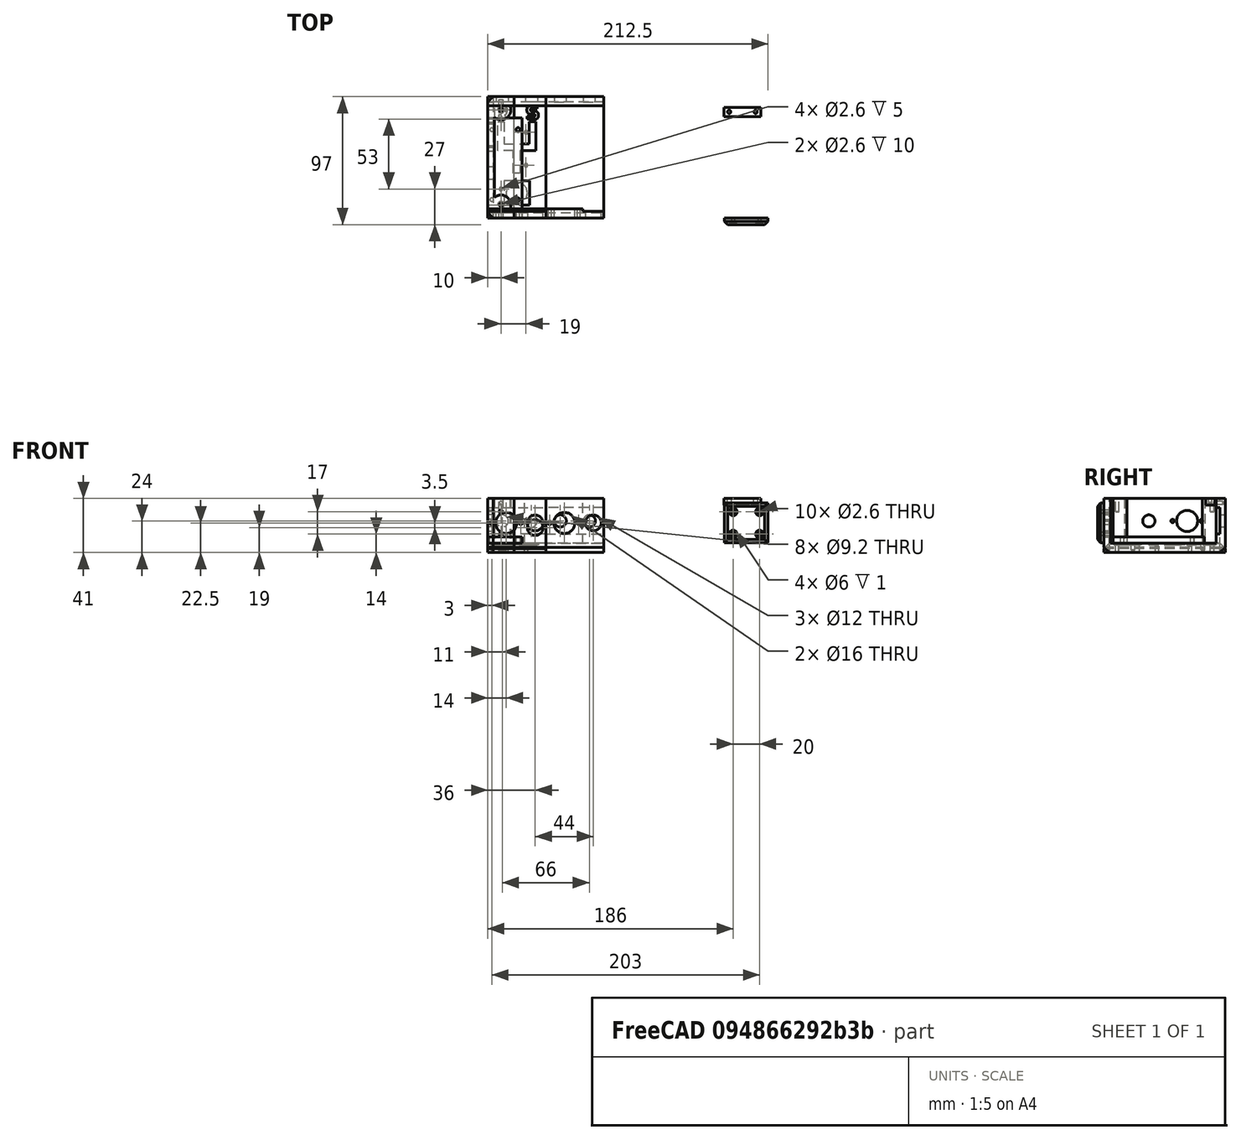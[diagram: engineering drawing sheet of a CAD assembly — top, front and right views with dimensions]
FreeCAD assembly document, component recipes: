
FREECAD ASSEMBLY — COMPONENT RECIPES ("loop-switcher")

This assembly document has 20 components, labeled P0..P19 below (a component is one placed body or linked part). 19 of them carry a construction recipe — the FreeCAD feature program that regenerates the part from scratch, quoted from this document or its linked companion documents; the rest are supplied as boundary geometry only. No exploded tour is included for this assembly.
COMPONENT P0 — recipe-attached ("base-module001", modeled in this document).
Construction recipe (the document's own serialized feature program — sketch geometry with constraints, then the solid features built on it; lengths are millimeters unless a unit is written):

FEATURE [Sketcher::SketchObject] Sketch
  ArcFitTolerance = 1e-06
  AttachmentSupport = -> [XY_Plane]
  FullyConstrained = true
  MakeInternals = false
  MapMode = 5
  sketch-geometry (4):
    g0: LineSegment StartX=0 StartY=0 StartZ=0 EndX=44 EndY=0 EndZ=0
    g1: LineSegment StartX=44 StartY=0 StartZ=0 EndX=44 EndY=92 EndZ=0
    g2: LineSegment StartX=44 StartY=92 StartZ=0 EndX=0 EndY=92 EndZ=0
    g3: LineSegment StartX=0 StartY=92 StartZ=0 EndX=0 EndY=0 EndZ=0
  constraints (11):
    c: Coincident(g0,g1)
    c: Coincident(g1,g2)
    c: Coincident(g2,g3)
    c: Coincident(g3,g0)
    c: Horizontal(g0)
    c: Horizontal(g2)
    c: Vertical(g1)
    c: Vertical(g3)
    c: Distance(g1,g3) = 44
    c: Distance(g0,g2) = 92
    c: Coincident(g0,g-1)
FEATURE [PartDesign::Pad] Pad
  Direction = (0,0,1)
  Length = 7
  Length2 = 10
  Profile = -> Sketch
  ReferenceAxis = -> Sketch [N_Axis]
  Refine = true
  Suppressed = false
  Type = 0
FEATURE [Sketcher::SketchObject] Sketch001
  ArcFitTolerance = 1e-06
  AttachmentSupport = -> [Pad]
  ExternalGeometry = -> [Pad]
  FullyConstrained = true
  MakeInternals = false
  MapMode = 5
  Placement = pos=(0,0,7) rot=(0,0,1;0rad)
  sketch-geometry (8):
    g0: LineSegment StartX=0 StartY=92 StartZ=0 EndX=0 EndY=85 EndZ=0
    g1: LineSegment StartX=0 StartY=85 StartZ=0 EndX=44 EndY=85 EndZ=0
    g2: LineSegment StartX=44 StartY=85 StartZ=0 EndX=44 EndY=92 EndZ=0
    g3: LineSegment StartX=44 StartY=92 StartZ=0 EndX=0 EndY=92 EndZ=0
    g4: LineSegment StartX=0 StartY=0 StartZ=0 EndX=44 EndY=0 EndZ=0
    g5: LineSegment StartX=44 StartY=0 StartZ=0 EndX=44 EndY=7 EndZ=0
    g6: LineSegment StartX=44 StartY=7 StartZ=0 EndX=0 EndY=7 EndZ=0
    g7: LineSegment StartX=0 StartY=7 StartZ=0 EndX=0 EndY=0 EndZ=0
  constraints (22):
    c: Coincident(g0,g1)
    c: Coincident(g1,g2)
    c: Coincident(g2,g3)
    c: Coincident(g3,g0)
    c: Vertical(g0)
    c: Vertical(g2)
    c: Horizontal(g1)
    c: Horizontal(g3)
    c: Distance(g0,g2) = 44
    c: Distance(g1,g3) = 7
    c: Coincident(g0,g-3)
    c: Coincident(g4,g5)
    c: Coincident(g5,g6)
    c: Coincident(g6,g7)
    c: Coincident(g7,g4)
    c: Horizontal(g4)
    c: Horizontal(g6)
    c: Vertical(g5)
    c: Vertical(g7)
    c: Distance(g5,g7) = 44
    c: Distance(g4,g6) = 7
    c: Coincident(g4,g-1)
FEATURE [PartDesign::Pad] Pad001
  BaseFeature = -> Pad
  Direction = (0,0,1)
  Length = 34
  Length2 = 10
  Profile = -> Sketch001
  ReferenceAxis = -> Sketch001 [N_Axis]
  Refine = true
  Suppressed = false
  Type = 0
FEATURE [Sketcher::SketchObject] Sketch002
  ArcFitTolerance = 1e-06
  AttachmentSupport = -> [Pad001]
  ExternalGeometry = -> [Pad001]
  FullyConstrained = true
  MakeInternals = false
  MapMode = 5
  Placement = pos=(0,92,0) rot=(0,0.707107,0.707107;3.14159rad)
  sketch-geometry (2):
    g0: Circle CenterX=-33 CenterY=24 CenterZ=0 NormalX=0 NormalY=0 NormalZ=1 AngleXU=0 Radius=4.6
    g1: Circle CenterX=-11 CenterY=24 CenterZ=0 NormalX=0 NormalY=0 NormalZ=1 AngleXU=0 Radius=4.6
  constraints (6):
    c: Diameter(g0) = 9.2
    c: Diameter(g1) = 9.2
    c: DistanceX(g-4,g0) = 11
    c: DistanceX(g1,g-3) = 11
    c: DistanceY(g0,g-4) = 17
    c: DistanceY(g1,g-3) = 17
FEATURE [PartDesign::Pocket] Pocket
  BaseFeature = -> Pad001
  Direction = (0,-1,2e-16)
  Length = 10
  Length2 = 5
  Profile = -> Sketch002
  ReferenceAxis = -> Sketch002 [N_Axis]
  Refine = true
  Suppressed = false
  Type = 0
FEATURE [Sketcher::SketchObject] Sketch003
  ArcFitTolerance = 1e-06
  AttachmentSupport = -> [Pocket]
  ExternalGeometry = -> [Pocket]
  FullyConstrained = true
  MakeInternals = false
  MapMode = 5
  Placement = pos=(0,85,0) rot=(1,0,0;1.5708rad)
  sketch-geometry (5):
    g0: LineSegment StartX=-1.7e-15 StartY=14 StartZ=0 EndX=44 EndY=14 EndZ=0
    g1: LineSegment StartX=44 StartY=14 StartZ=0 EndX=44 EndY=34 EndZ=0
    g2: LineSegment StartX=44 StartY=34 StartZ=0 EndX=0 EndY=34 EndZ=0
    g3: LineSegment StartX=-1.7e-15 StartY=34 StartZ=0 EndX=-1.7e-15 EndY=14 EndZ=0
    g4: GeomPoint [constr] X=22 Y=24 Z=0
  constraints (13):
    c: Coincident(g0,g1)
    c: Coincident(g1,g2)
    c: Coincident(g2,g3)
    c: Coincident(g3,g0)
    c: Horizontal(g0)
    c: Horizontal(g2)
    c: Vertical(g1)
    c: Vertical(g3)
    c: Symmetric(g2,g0,g4)
    c: Distance(g1,g3) = 44
    c: Distance(g0,g2) = 20
    c: DistanceX(g4,g-4) = 22
    c: DistanceY(g4,g-4) = 17
FEATURE [PartDesign::Pocket] Pocket001
  BaseFeature = -> Pocket
  Direction = (0,1,-2e-16)
  Length = 3
  Length2 = 5
  Profile = -> Sketch003
  ReferenceAxis = -> Sketch003 [N_Axis]
  Refine = true
  Suppressed = false
  Type = 0
FEATURE [PartDesign::Chamfer] Chamfer
  Angle = 45
  Base = -> Pocket001 [Edge1,Edge3]
  BaseFeature = -> Pocket001
  ChamferType = 0
  FlipDirection = false
  Refine = true
  Size = 4
  Size2 = 1
  SupportTransform = false
  Suppressed = false
  UseAllEdges = false
FEATURE [PartDesign::Body] Body  label="base-module"
  AllowCompound = false
  Group = -> [Sketch,Pad,Sketch001,Pad001,Sketch002,Pocket,Sketch003,Pocket001,Chamfer]
  Origin = -> Origin
  Tip = -> Chamfer
COMPONENT P1 — same part as P0; its construction recipe is shown at P0.
COMPONENT P2 — same part as P0; its construction recipe is shown at P0.
COMPONENT P3 — same part as P0; its construction recipe is shown at P0.
COMPONENT P4 — same part as P0; its construction recipe is shown at P0.
COMPONENT P5 — recipe-attached ("lid-module001", modeled in this document).
Construction recipe (the document's own serialized feature program — sketch geometry with constraints, then the solid features built on it; lengths are millimeters unless a unit is written):

FEATURE [Sketcher::SketchObject] Sketch004
  ArcFitTolerance = 1e-06
  AttachmentSupport = -> [XY_Plane003]
  FullyConstrained = true
  MakeInternals = false
  MapMode = 5
  sketch-geometry (4):
    g0: LineSegment StartX=0 StartY=0 StartZ=0 EndX=44 EndY=0 EndZ=0
    g1: LineSegment StartX=44 StartY=0 StartZ=0 EndX=44 EndY=92 EndZ=0
    g2: LineSegment StartX=44 StartY=92 StartZ=0 EndX=0 EndY=92 EndZ=0
    g3: LineSegment StartX=0 StartY=92 StartZ=0 EndX=0 EndY=0 EndZ=0
  constraints (11):
    c: Coincident(g0,g1)
    c: Coincident(g1,g2)
    c: Coincident(g2,g3)
    c: Coincident(g3,g0)
    c: Horizontal(g0)
    c: Horizontal(g2)
    c: Vertical(g1)
    c: Vertical(g3)
    c: Distance(g1,g3) = 44
    c: Distance(g0,g2) = 92
    c: Coincident(g0,g-1)
FEATURE [PartDesign::Pad] Pad002
  Direction = (0,0,1)
  Length = 7
  Length2 = 10
  Profile = -> Sketch004
  ReferenceAxis = -> Sketch004 [N_Axis]
  Refine = true
  Suppressed = false
  Type = 0
FEATURE [PartDesign::Chamfer] Chamfer001
  Angle = 45
  Base = -> Pad002 [Edge4,Edge10]
  BaseFeature = -> Pad002
  ChamferType = 0
  FlipDirection = false
  Refine = true
  Size = 4
  Size2 = 1
  SupportTransform = false
  Suppressed = false
  UseAllEdges = false
FEATURE [Sketcher::SketchObject] Sketch005
  ArcFitTolerance = 1e-06
  AttachmentOffset = pos=(0,5,0) rot=(0,0,1;0rad)
  AttachmentSupport = -> [Chamfer001]
  ExternalGeometry = -> [Chamfer001]
  FullyConstrained = true
  MakeInternals = false
  MapMode = 5
  Placement = pos=(0,5,7) rot=(0,0,1;0rad)
  sketch-geometry (12):
    g0: LineSegment StartX=7.5 StartY=68 StartZ=0 EndX=12.5 EndY=68 EndZ=0
    g1: LineSegment StartX=12.5 StartY=68 StartZ=0 EndX=12.5 EndY=51.1 EndZ=0
    g2: LineSegment StartX=12.5 StartY=51.1 StartZ=0 EndX=31.5 EndY=51.1 EndZ=0
    g3: LineSegment StartX=31.5 StartY=51.1 StartZ=0 EndX=31.5 EndY=68 EndZ=0
    g4: LineSegment StartX=31.5 StartY=68 StartZ=0 EndX=36.5 EndY=68 EndZ=0
    g5: LineSegment StartX=36.5 StartY=68 StartZ=0 EndX=36.5 EndY=46.1 EndZ=0
    g6: LineSegment StartX=36.5 StartY=46.1 StartZ=0 EndX=24.5 EndY=46.1 EndZ=0
    g7: LineSegment StartX=24.5 StartY=46.1 StartZ=0 EndX=24.5 EndY=29 EndZ=0
    g8: LineSegment StartX=24.5 StartY=29 StartZ=0 EndX=19.5 EndY=29 EndZ=0
    g9: LineSegment StartX=19.5 StartY=29 StartZ=0 EndX=19.5 EndY=46.1 EndZ=0
    g10: LineSegment StartX=19.5 StartY=46.1 StartZ=0 EndX=7.5 EndY=46.1 EndZ=0
    g11: LineSegment StartX=7.5 StartY=46.1 StartZ=0 EndX=7.5 EndY=68 EndZ=0
  constraints (36):
    c: Coincident(g0,g1)
    c: Coincident(g1,g2)
    c: Coincident(g2,g3)
    c: Coincident(g3,g4)
    c: Horizontal(g4)
    c: Coincident(g4,g5)
    c: Coincident(g5,g6)
    c: Coincident(g6,g7)
    c: Vertical(g7)
    c: Coincident(g7,g8)
    c: Coincident(g8,g9)
    c: Coincident(g9,g10)
    c: Coincident(g10,g11)
    c: Coincident(g11,g0)
    c: DistanceX(g0,g0) = 5
    c: DistanceX(g3,g4) = 5
    c: DistanceY(g0,g0) = 0
    c: DistanceY(g3,g0) = 0
    c: DistanceX(g10,g0) = 0
    c: DistanceX(g5,g4) = 0
    c: DistanceX(g2,g3) = 0
    c: DistanceX(g1,g0) = 0
    c: DistanceY(g2,g1) = 0
    c: DistanceY(g9,g1) = 5
    c: DistanceY(g5,g10) = 0
    c: DistanceX(g8,g7) = 5
    c: DistanceY(g7,g8) = 0
    c: DistanceY(g5,g6) = 0
    c: DistanceX(g8,g9) = 0
    c: DistanceX(g4,g-4) = 7.5
    c: DistanceX(g-3,g0) = 7.5
    c: DistanceX(g-1,g8) = 19.5
    c: DistanceY(g0,g-3) = 15
    c: DistanceY(g-1,g8) = 29
    c: DistanceY(g1,g0) = 16.9
    c: DistanceY(g10,g1) = 5
FEATURE [PartDesign::Pocket] Pocket002
  BaseFeature = -> Chamfer001
  Direction = (0,0,-1)
  Length = 1
  Length2 = 5
  Profile = -> Sketch005
  ReferenceAxis = -> Sketch005 [N_Axis]
  Refine = true
  Suppressed = false
  Type = 0
FEATURE [Sketcher::SketchObject] Sketch006
  ArcFitTolerance = 1e-06
  AttachmentSupport = -> [Pocket002]
  ExternalGeometry = -> [Pocket002]
  FullyConstrained = true
  MakeInternals = false
  MapMode = 5
  Placement = pos=(0,0,7) rot=(0,0,1;0rad)
  sketch-geometry (1):
    g0: Circle CenterX=22 CenterY=19 CenterZ=0 NormalX=0 NormalY=0 NormalZ=1 AngleXU=0 Radius=8
  constraints (3):
    c: Diameter(g0) = 16
    c: DistanceX(g-1,g0) = 22
    c: DistanceY(g-4,g0) = 15
FEATURE [PartDesign::Pocket] Pocket003
  BaseFeature = -> Pocket002
  Direction = (0,0,-1)
  Length = 10
  Length2 = 5
  Profile = -> Sketch006
  ReferenceAxis = -> Sketch006 [N_Axis]
  Refine = true
  Suppressed = false
  Type = 0
FEATURE [Sketcher::SketchObject] Sketch007
  ArcFitTolerance = 1e-06
  AttachmentSupport = -> [Pocket003]
  ExternalGeometry = -> [Pocket003]
  FullyConstrained = true
  MakeInternals = false
  MapMode = 5
  Placement = pos=(0,0,7) rot=(0,0,1;0rad)
  sketch-geometry (5):
    g0: LineSegment StartX=12.25 StartY=9.75 StartZ=0 EndX=31.75 EndY=9.75 EndZ=0
    g1: LineSegment StartX=31.75 StartY=9.75 StartZ=0 EndX=31.75 EndY=28.25 EndZ=0
    g2: LineSegment StartX=31.75 StartY=28.25 StartZ=0 EndX=12.25 EndY=28.25 EndZ=0
    g3: LineSegment StartX=12.25 StartY=28.25 StartZ=0 EndX=12.25 EndY=9.75 EndZ=0
    g4: GeomPoint [constr] X=22 Y=19 Z=0
  constraints (13):
    c: Coincident(g0,g1)
    c: Coincident(g1,g2)
    c: Coincident(g2,g3)
    c: Coincident(g3,g0)
    c: Horizontal(g0)
    c: Horizontal(g2)
    c: Vertical(g1)
    c: Vertical(g3)
    c: Symmetric(g2,g0,g4)
    c: Distance(g1,g3) = 19.5
    c: Distance(g0,g2) = 18.5
    c: DistanceY(g-3,g4) = 15
    c: DistanceX(g4,g-3) = 22
FEATURE [PartDesign::Pocket] Pocket004
  BaseFeature = -> Pocket003
  Direction = (0,0,-1)
  Length = 1
  Length2 = 5
  Profile = -> Sketch007
  ReferenceAxis = -> Sketch007 [N_Axis]
  Refine = true
  Suppressed = false
  Type = 0
FEATURE [Part::Part2DObjectPython] ShapeString  # Draft 2D object (typed FeaturePython)
  FontFile = <path>
  Fuse = false
  Justification = 4
  JustificationReference = 0
  KeepLeftMargin = false
  MakeFace = true
  ObliqueAngle = 0
  Placement = pos=(34,80,7) rot=(0,0,1;0rad)
  ScaleToSize = true
  Size = 10
  String = S
  Tracking = 0
FEATURE [PartDesign::Pocket] Pocket005
  BaseFeature = -> Pocket004
  Direction = (0,0,-1)
  Length = 1
  Length2 = 5
  Profile = -> ShapeString
  ReferenceAxis = -> ShapeString [N_Axis]
  Refine = true
  Suppressed = false
  Type = 0
FEATURE [Part::Part2DObjectPython] ShapeString001  # Draft 2D object (typed FeaturePython)
  FontFile = <path>
  Fuse = false
  Justification = 4
  JustificationReference = 0
  KeepLeftMargin = false
  MakeFace = true
  ObliqueAngle = 0
  Placement = pos=(10,80,7) rot=(0,0,1;0rad)
  ScaleToSize = true
  Size = 10
  String = R
  Tracking = 0
FEATURE [PartDesign::Pocket] Pocket006
  BaseFeature = -> Pocket005
  Direction = (0,0,-1)
  Length = 1
  Length2 = 5
  Profile = -> ShapeString001
  ReferenceAxis = -> ShapeString001 [N_Axis]
  Refine = true
  Suppressed = false
  Type = 0
FEATURE [PartDesign::Body] Body001  label="lid-module"
  AllowCompound = false
  Group = -> [Sketch004,Pad002,Chamfer001,Sketch005,Pocket002,Sketch006,Pocket003,Sketch007,Pocket004,ShapeString,Pocket005,ShapeString001,Pocket006]
  Origin = -> Origin003
  Tip = -> Pocket006
COMPONENT P6 — same part as P5; its construction recipe is shown at P5.
COMPONENT P7 — same part as P5; its construction recipe is shown at P5.
COMPONENT P8 — same part as P5; its construction recipe is shown at P5.
COMPONENT P9 — same part as P5; its construction recipe is shown at P5.
COMPONENT P10 — same part as P5; its construction recipe is shown at P5.
COMPONENT P11 — recipe-attached ("lid-side001", modeled in this document).
Construction recipe (the document's own serialized feature program — sketch geometry with constraints, then the solid features built on it; lengths are millimeters unless a unit is written):

FEATURE [Sketcher::SketchObject] Sketch015
  ArcFitTolerance = 1e-06
  AttachmentSupport = -> [XY_Plane012]
  FullyConstrained = true
  MakeInternals = false
  MapMode = 5
  sketch-geometry (4):
    g0: LineSegment StartX=0 StartY=0 StartZ=0 EndX=20 EndY=0 EndZ=0
    g1: LineSegment StartX=20 StartY=0 StartZ=0 EndX=20 EndY=92 EndZ=0
    g2: LineSegment StartX=20 StartY=92 StartZ=0 EndX=0 EndY=92 EndZ=0
    g3: LineSegment StartX=0 StartY=92 StartZ=0 EndX=0 EndY=0 EndZ=0
  constraints (11):
    c: Coincident(g0,g1)
    c: Coincident(g1,g2)
    c: Coincident(g2,g3)
    c: Coincident(g3,g0)
    c: Horizontal(g0)
    c: Horizontal(g2)
    c: Vertical(g1)
    c: Vertical(g3)
    c: Distance(g1,g3) = 20
    c: Distance(g0,g2) = 92
    c: Coincident(g0,g-1)
FEATURE [PartDesign::Pad] Pad006
  Direction = (0,0,1)
  Length = 7
  Length2 = 10
  Profile = -> Sketch015
  ReferenceAxis = -> Sketch015 [N_Axis]
  Refine = true
  Suppressed = false
  Type = 0
FEATURE [PartDesign::Chamfer] Chamfer003
  Angle = 45
  Base = -> Pad006 [Edge10,Edge12,Edge4,Edge1,Edge8]
  BaseFeature = -> Pad006
  ChamferType = 0
  FlipDirection = false
  Refine = true
  Size = 4
  Size2 = 1
  SupportTransform = false
  Suppressed = false
  UseAllEdges = false
FEATURE [Sketcher::SketchObject] Sketch016
  ArcFitTolerance = 1e-06
  AttachmentSupport = -> [Chamfer003]
  ExternalGeometry = -> [Chamfer003]
  FullyConstrained = true
  MakeInternals = false
  MapMode = 5
  Placement = pos=(0,0,7) rot=(0,0,1;0rad)
  sketch-geometry (2):
    g0: Circle CenterX=10 CenterY=10 CenterZ=0 NormalX=0 NormalY=0 NormalZ=1 AngleXU=0 Radius=1.3
    g1: Circle CenterX=14 CenterY=82 CenterZ=0 NormalX=0 NormalY=0 NormalZ=1 AngleXU=0 Radius=1.3
  constraints (6):
    c: Diameter(g0) = 2.6
    c: Diameter(g1) = 2.6
    c: DistanceY(g1,g-3) = 10
    c: DistanceX(g-3,g1) = 10
    c: DistanceX(g-1,g0) = 10
    c: DistanceY(g-1,g0) = 10
FEATURE [PartDesign::Pocket] Pocket011
  BaseFeature = -> Chamfer003
  Direction = (0,0,-1)
  Length = 7
  Length2 = 5
  Profile = -> Sketch016
  ReferenceAxis = -> Sketch016 [N_Axis]
  Refine = true
  Suppressed = false
  Type = 0
FEATURE [Sketcher::SketchObject] Sketch017
  ArcFitTolerance = 1e-06
  AttachmentSupport = -> [Pocket011]
  FullyConstrained = true
  MakeInternals = false
  MapMode = 5
  Placement = pos=(0,0,7) rot=(0,0,1;0rad)
  sketch-geometry (2):
    g0: Circle CenterX=10 CenterY=10 CenterZ=0 NormalX=0 NormalY=0 NormalZ=1 AngleXU=0 Radius=2.5
    g1: Circle CenterX=10 CenterY=82 CenterZ=0 NormalX=0 NormalY=0 NormalZ=1 AngleXU=0 Radius=2.5
  constraints (6):
    c: Diameter(g0) = 5
    c: Diameter(g1) = 5
    c: DistanceY(g1,g-3) = 10
    c: DistanceY(g-1,g0) = 10
    c: DistanceX(g-1,g0) = 10
    c: DistanceX(g-3,g1) = 10
FEATURE [PartDesign::Pocket] Pocket012
  BaseFeature = -> Pocket011
  Direction = (0,0,-1)
  Length = 1
  Length2 = 5
  Profile = -> Sketch017
  ReferenceAxis = -> Sketch017 [N_Axis]
  Refine = true
  Suppressed = false
  Type = 0
FEATURE [PartDesign::Body] Body004  label="lid-side"
  AllowCompound = false
  Group = -> [Sketch015,Pad006,Chamfer003,Sketch016,Pocket011,Sketch017,Pocket012]
  Origin = -> Origin012
  Tip = -> Pocket012
COMPONENT P12 — same part as P11; its construction recipe is shown at P11.
COMPONENT P13 — recipe-attached ("lid-split-left001", modeled in this document).
Construction recipe (the document's own serialized feature program — sketch geometry with constraints, then the solid features built on it; lengths are millimeters unless a unit is written):

FEATURE [PartDesign::FeatureBase] Clone001
  BaseFeature = -> Body001
  Suppressed = false
FEATURE [Sketcher::SketchObject] Sketch018
  ArcFitTolerance = 1e-06
  AttachmentSupport = -> [Clone001]
  ExternalGeometry = -> [Clone001]
  FullyConstrained = true
  MakeInternals = false
  MapMode = 5
  Placement = pos=(0,0,0) rot=(1,0,0;3.14159rad)
  sketch-geometry (2):
    g0: Circle CenterX=29 CenterY=-40 CenterZ=0 NormalX=0 NormalY=0 NormalZ=1 AngleXU=0 Radius=1.3
    g1: Circle CenterX=29 CenterY=-65 CenterZ=0 NormalX=0 NormalY=0 NormalZ=1 AngleXU=0 Radius=1.3
  constraints (6):
    c: Diameter(g0) = 2.6
    c: Diameter(g1) = 2.6
    c: DistanceX(g0,g1) = 0
    c: DistanceY(g1,g0) = 25
    c: DistanceY(g0,g-3) = 40
    c: DistanceX(g0,g-3) = 15
FEATURE [PartDesign::Pocket] Pocket013
  BaseFeature = -> Clone001
  Direction = (0,0,1)
  Length = 5
  Length2 = 5
  Profile = -> Sketch018
  ReferenceAxis = -> Sketch018 [N_Axis]
  Refine = true
  Suppressed = false
  Type = 0
FEATURE [PartDesign::Body] Body005  label="lid-split-left"
  AllowCompound = false
  Group = -> [Clone001,Sketch018,Pocket013]
  Origin = -> Origin013
  Tip = -> Pocket013
COMPONENT P14 — recipe-attached ("lid-split-right001", modeled in this document).
Construction recipe (the document's own serialized feature program — sketch geometry with constraints, then the solid features built on it; lengths are millimeters unless a unit is written):

FEATURE [PartDesign::FeatureBase] Clone002
  BaseFeature = -> Body001
  Suppressed = false
FEATURE [Sketcher::SketchObject] Sketch019
  ArcFitTolerance = 1e-06
  AttachmentSupport = -> [Clone002]
  FullyConstrained = true
  MakeInternals = false
  MapMode = 5
  Placement = pos=(0,0,0) rot=(1,0,0;3.14159rad)
  sketch-geometry (2):
    g0: Circle CenterX=15 CenterY=-40 CenterZ=0 NormalX=0 NormalY=0 NormalZ=1 AngleXU=0 Radius=1.3
    g1: Circle CenterX=15 CenterY=-65 CenterZ=0 NormalX=0 NormalY=0 NormalZ=1 AngleXU=0 Radius=1.3
  constraints (6):
    c: Diameter(g0) = 2.6
    c: Diameter(g1) = 2.6
    c: DistanceX(g0,g1) = 0
    c: DistanceY(g1,g0) = 25
    c: DistanceX(g-1,g0) = 15
    c: DistanceY(g0,g-1) = 40
FEATURE [PartDesign::Pocket] Pocket014
  BaseFeature = -> Clone002
  Direction = (0,0,1)
  Length = 5
  Length2 = 5
  Profile = -> Sketch019
  ReferenceAxis = -> Sketch019 [N_Axis]
  Refine = true
  Suppressed = false
  Type = 0
FEATURE [PartDesign::Body] Body006  label="lid-split-right"
  AllowCompound = false
  Group = -> [Clone002,Sketch019,Pocket014]
  Origin = -> Origin014
  Tip = -> Pocket014
COMPONENT P15 — recipe-attached ("power-input-base-module001", modeled in this document).
Construction recipe (the document's own serialized feature program — sketch geometry with constraints, then the solid features built on it; lengths are millimeters unless a unit is written):

FEATURE [PartDesign::FeatureBase] Clone005
  BaseFeature = -> Body
  Suppressed = false
FEATURE [Sketcher::SketchObject] Sketch031
  ArcFitTolerance = 1e-06
  AttachmentSupport = -> [Clone005]
  ExternalGeometry = -> [Clone005]
  FullyConstrained = true
  MakeInternals = false
  MapMode = 5
  Placement = pos=(0,0,0) rot=(1,0,0;1.5708rad)
  sketch-geometry (1):
    g0: Circle CenterX=36 CenterY=19 CenterZ=0 NormalX=0 NormalY=0 NormalZ=1 AngleXU=0 Radius=6
  constraints (3):
    c: Diameter(g0) = 12
    c: DistanceX(g0,g-3) = 8
    c: DistanceY(g-3,g0) = 15
FEATURE [PartDesign::Pocket] Pocket023
  BaseFeature = -> Clone005
  Direction = (0,1,-2e-16)
  Length = 7
  Length2 = 5
  Profile = -> Sketch031
  ReferenceAxis = -> Sketch031 [N_Axis]
  Refine = true
  Suppressed = false
  Type = 0
FEATURE [Sketcher::SketchObject] Sketch032
  ArcFitTolerance = 1e-06
  AttachmentSupport = -> [Pocket023]
  ExternalGeometry = -> [Pocket023]
  FullyConstrained = true
  MakeInternals = false
  MapMode = 5
  Placement = pos=(0,7,0) rot=(0,0.707107,0.707107;3.14159rad)
  sketch-geometry (4):
    g0: LineSegment StartX=-44 StartY=41 StartZ=0 EndX=-44 EndY=7 EndZ=0
    g1: LineSegment StartX=-44 StartY=7 StartZ=0 EndX=0 EndY=7 EndZ=0
    g2: LineSegment StartX=0 StartY=7 StartZ=0 EndX=0 EndY=41 EndZ=0
    g3: LineSegment StartX=0 StartY=41 StartZ=0 EndX=-44 EndY=41 EndZ=0
  constraints (10):
    c: Coincident(g0,g1)
    c: Coincident(g1,g2)
    c: Coincident(g2,g3)
    c: Coincident(g3,g0)
    c: Vertical(g0)
    c: Vertical(g2)
    c: Horizontal(g1)
    c: Horizontal(g3)
    c: Coincident(g0,g-3)
    c: Coincident(g1,g-4)
FEATURE [PartDesign::Pocket] Pocket024
  BaseFeature = -> Pocket023
  Direction = (0,-1,2e-16)
  Length = 2
  Length2 = 5
  Profile = -> Sketch032
  ReferenceAxis = -> Sketch032 [N_Axis]
  Refine = true
  Suppressed = false
  Type = 0
FEATURE [PartDesign::Body] Body010  label="power-input-base-module"
  AllowCompound = false
  Group = -> [Clone005,Sketch031,Pocket023,Sketch032,Pocket024]
  Origin = -> Origin024
  Tip = -> Pocket024
COMPONENT P16 — geometry summary ("right-split001"; no construction recipe available for this part):
  bounding box: 92.0 x 44.0 x 41.0 mm
  tessellated surface: 3,316 triangles
  volume: 45250 mm^3 (27% of its bounding box)
COMPONENT P17 — recipe-attached ("side001", modeled in this document).
Construction recipe (the document's own serialized feature program — sketch geometry with constraints, then the solid features built on it; lengths are millimeters unless a unit is written):

FEATURE [Sketcher::SketchObject] Sketch008
  ArcFitTolerance = 1e-06
  AttachmentSupport = -> [XY_Plane006]
  FullyConstrained = true
  MakeInternals = false
  MapMode = 5
  sketch-geometry (4):
    g0: LineSegment StartX=0 StartY=0 StartZ=0 EndX=20 EndY=0 EndZ=0
    g1: LineSegment StartX=20 StartY=0 StartZ=0 EndX=20 EndY=92 EndZ=0
    g2: LineSegment StartX=20 StartY=92 StartZ=0 EndX=0 EndY=92 EndZ=0
    g3: LineSegment StartX=0 StartY=92 StartZ=0 EndX=0 EndY=0 EndZ=0
  constraints (11):
    c: Coincident(g0,g1)
    c: Coincident(g1,g2)
    c: Coincident(g2,g3)
    c: Coincident(g3,g0)
    c: Horizontal(g0)
    c: Horizontal(g2)
    c: Vertical(g1)
    c: Vertical(g3)
    c: Distance(g1,g3) = 20
    c: Distance(g0,g2) = 92
    c: Coincident(g0,g-1)
FEATURE [PartDesign::Pad] Pad003
  Direction = (0,0,1)
  Length = 7
  Length2 = 10
  Profile = -> Sketch008
  ReferenceAxis = -> Sketch008 [N_Axis]
  Refine = true
  Suppressed = false
  Type = 0
FEATURE [Sketcher::SketchObject] Sketch009
  ArcFitTolerance = 1e-06
  AttachmentSupport = -> [Pad003]
  ExternalGeometry = -> [Pad003]
  FullyConstrained = true
  MakeInternals = false
  MapMode = 5
  Placement = pos=(0,0,7) rot=(0,0,1;0rad)
  sketch-geometry (12):
    g0: LineSegment StartX=20 StartY=92 StartZ=0 EndX=0 EndY=92 EndZ=0
    g1: LineSegment StartX=0 StartY=92 StartZ=0 EndX=0 EndY=85 EndZ=0
    g2: LineSegment StartX=0 StartY=85 StartZ=0 EndX=20 EndY=85 EndZ=0
    g3: LineSegment StartX=20 StartY=85 StartZ=0 EndX=20 EndY=92 EndZ=0
    g4: LineSegment StartX=0 StartY=0 StartZ=0 EndX=20 EndY=0 EndZ=0
    g5: LineSegment StartX=20 StartY=0 StartZ=0 EndX=20 EndY=7 EndZ=0
    g6: LineSegment StartX=20 StartY=7 StartZ=0 EndX=0 EndY=7 EndZ=0
    g7: LineSegment StartX=0 StartY=7 StartZ=0 EndX=0 EndY=0 EndZ=0
    g8: LineSegment StartX=0 StartY=7 StartZ=0 EndX=5 EndY=7 EndZ=0
    g9: LineSegment StartX=5 StartY=7 StartZ=0 EndX=5 EndY=85 EndZ=0
    g10: LineSegment StartX=5 StartY=85 StartZ=0 EndX=0 EndY=85 EndZ=0
    g11: LineSegment StartX=0 StartY=85 StartZ=0 EndX=0 EndY=7 EndZ=0
  constraints (33):
    c: Coincident(g0,g1)
    c: Coincident(g1,g2)
    c: Coincident(g2,g3)
    c: Coincident(g3,g0)
    c: Horizontal(g0)
    c: Horizontal(g2)
    c: Vertical(g1)
    c: Vertical(g3)
    c: Distance(g0,g2) = 7
    c: Coincident(g0,g-4)
    c: PointOnObject(g1,g-2)
    c: Coincident(g4,g5)
    c: Coincident(g5,g6)
    c: Coincident(g6,g7)
    c: Coincident(g7,g4)
    c: Horizontal(g4)
    c: Horizontal(g6)
    c: Vertical(g5)
    c: Vertical(g7)
    c: Distance(g4,g6) = 7
    c: Coincident(g4,g-1)
    c: PointOnObject(g5,g-4)
    c: Coincident(g8,g9)
    c: Coincident(g9,g10)
    c: Coincident(g10,g11)
    c: Coincident(g11,g8)
    c: Horizontal(g8)
    c: Horizontal(g10)
    c: Vertical(g9)
    c: Vertical(g11)
    c: Distance(g9,g11) = 5
    c: Coincident(g8,g6)
    c: PointOnObject(g9,g2)
FEATURE [PartDesign::Pad] Pad004
  BaseFeature = -> Pad003
  Direction = (0,0,1)
  Length = 34
  Length2 = 10
  Profile = -> Sketch009
  ReferenceAxis = -> Sketch009 [N_Axis]
  Refine = true
  Suppressed = false
  Type = 0
FEATURE [Sketcher::SketchObject] Sketch010
  ArcFitTolerance = 1e-06
  AttachmentSupport = -> [Pad004]
  ExternalGeometry = -> [Pad004]
  FullyConstrained = true
  MakeInternals = false
  MapMode = 5
  Placement = pos=(0,0,7) rot=(0,0,1;0rad)
  sketch-geometry (2):
    g0: Circle CenterX=10 CenterY=82 CenterZ=0 NormalX=0 NormalY=0 NormalZ=1 AngleXU=0 Radius=7.5
    g1: Circle CenterX=10 CenterY=10 CenterZ=0 NormalX=0 NormalY=0 NormalZ=1 AngleXU=0 Radius=7.5
  constraints (6):
    c: Diameter(g0) = 15
    c: DistanceY(g0,g-3) = 10
    c: DistanceX(g-3,g0) = 10
    c: Diameter(g1) = 15
    c: DistanceY(g-1,g1) = 10
    c: DistanceX(g-1,g1) = 10
FEATURE [PartDesign::Pad] Pad005
  BaseFeature = -> Pad004
  Direction = (0,0,1)
  Length = 34
  Length2 = 10
  Profile = -> Sketch010
  ReferenceAxis = -> Sketch010 [N_Axis]
  Refine = true
  Suppressed = false
  Type = 0
FEATURE [Sketcher::SketchObject] Sketch011
  ArcFitTolerance = 1e-06
  AttachmentSupport = -> [Pad005]
  ExternalGeometry = -> [Pad005]
  FullyConstrained = true
  MakeInternals = false
  MapMode = 5
  Placement = pos=(0,0,41) rot=(0,0,1;0rad)
  sketch-geometry (2):
    g0: Circle CenterX=10 CenterY=82 CenterZ=0 NormalX=0 NormalY=0 NormalZ=1 AngleXU=0 Radius=1.3
    g1: Circle CenterX=10 CenterY=10 CenterZ=0 NormalX=0 NormalY=0 NormalZ=1 AngleXU=0 Radius=1.3
  constraints (6):
    c: Diameter(g0) = 2.6
    c: Diameter(g1) = 2.6
    c: DistanceY(g-1,g1) = 10
    c: DistanceX(g-1,g1) = 10
    c: DistanceY(g0,g-3) = 10
    c: DistanceX(g-3,g0) = 10
FEATURE [PartDesign::Pocket] Pocket007
  BaseFeature = -> Pad005
  Direction = (0,0,-1)
  Length = 10
  Length2 = 5
  Profile = -> Sketch011
  ReferenceAxis = -> Sketch011 [N_Axis]
  Refine = true
  Suppressed = false
  Type = 0
FEATURE [PartDesign::Chamfer] Chamfer002
  Angle = 45
  Base = -> Pocket007 [Edge1,Edge7,Edge4,Edge14,Edge3]
  BaseFeature = -> Pocket007
  ChamferType = 0
  FlipDirection = false
  Refine = true
  Size = 4
  Size2 = 1
  SupportTransform = false
  Suppressed = false
  UseAllEdges = false
FEATURE [Sketcher::SketchObject] Sketch021
  ArcFitTolerance = 1e-06
  AttachmentSupport = -> [Chamfer002]
  ExternalGeometry = -> [Chamfer002]
  FullyConstrained = true
  MakeInternals = false
  MapMode = 5
  Placement = pos=(0,0,0) rot=(0.57735,-0.57735,-0.57735;2.0944rad)
  sketch-geometry (4):
    g0: Circle CenterX=-34 CenterY=24 CenterZ=0 NormalX=0 NormalY=0 NormalZ=1 AngleXU=0 Radius=4.6
    g1: Circle CenterX=-63 CenterY=24 CenterZ=0 NormalX=0 NormalY=0 NormalZ=1 AngleXU=0 Radius=8
    g2: Circle CenterX=-52 CenterY=24 CenterZ=0 NormalX=0 NormalY=0 NormalZ=1 AngleXU=0 Radius=1.3
    g3: Circle CenterX=-74 CenterY=24 CenterZ=0 NormalX=0 NormalY=0 NormalZ=1 AngleXU=0 Radius=1.3
  constraints (12):
    c: Diameter(g0) = 9.2
    c: DistanceY(g0,g-3) = 17
    c: Diameter(g1) = 16
    c: Diameter(g2) = 2.6
    c: Diameter(g3) = 2.6
    c: DistanceY(g2,g1) = 0
    c: DistanceY(g3,g1) = 0
    c: DistanceX(g1,g2) = 11
    c: DistanceX(g3,g1) = 11
    c: DistanceX(g0,g-3) = 30
    c: DistanceX(g-3,g1) = 25
    c: DistanceY(g3,g-3) = 17
FEATURE [PartDesign::Pocket] Pocket015
  BaseFeature = -> Chamfer002
  Direction = (1,0,0)
  Length = 7
  Length2 = 5
  Profile = -> Sketch021
  ReferenceAxis = -> Sketch021 [N_Axis]
  Refine = true
  Suppressed = false
  Type = 0
FEATURE [PartDesign::Body] Body002  label="side"
  AllowCompound = false
  Group = -> [Sketch008,Pad003,Sketch009,Pad004,Sketch010,Pad005,Sketch011,Pocket007,Chamfer002,Sketch021,Pocket015]
  Origin = -> Origin006
  Tip = -> Pocket015
COMPONENT P18 — same part as P17; its construction recipe is shown at P17.
COMPONENT P19 — recipe-attached ("split-module001", modeled in this document).
Construction recipe (the document's own serialized feature program — sketch geometry with constraints, then the solid features built on it; lengths are millimeters unless a unit is written):

FEATURE [PartDesign::FeatureBase] Clone
  BaseFeature = -> Body
  Suppressed = false
FEATURE [Sketcher::SketchObject] Sketch012
  ArcFitTolerance = 1e-06
  AttachmentSupport = -> [Clone]
  ExternalGeometry = -> [Clone]
  FullyConstrained = true
  MakeInternals = false
  MapMode = 5
  Placement = pos=(0,0,7) rot=(0,0,1;0rad)
  sketch-geometry (2):
    g0: Circle CenterX=34 CenterY=75 CenterZ=0 NormalX=0 NormalY=0 NormalZ=1 AngleXU=0 Radius=1.3
    g1: Circle CenterX=34 CenterY=22 CenterZ=0 NormalX=0 NormalY=0 NormalZ=1 AngleXU=0 Radius=1.3
  constraints (6):
    c: Diameter(g0) = 2.6
    c: Diameter(g1) = 2.6
    c: DistanceY(g0,g-4) = 10
    c: DistanceX(g0,g-4) = 10
    c: DistanceY(g-3,g1) = 15
    c: DistanceX(g1,g-3) = 10
FEATURE [PartDesign::Pocket] Pocket008
  BaseFeature = -> Clone
  Direction = (0,0,-1)
  Length = 5
  Length2 = 5
  Profile = -> Sketch012
  ReferenceAxis = -> Sketch012 [N_Axis]
  Refine = true
  Suppressed = false
  Type = 0
FEATURE [Sketcher::SketchObject] Sketch013
  ArcFitTolerance = 1e-06
  AttachmentSupport = -> [Pocket008]
  ExternalGeometry = -> [Pocket008]
  FullyConstrained = true
  MakeInternals = false
  MapMode = 5
  Placement = pos=(0,0,0) rot=(1,0,0;1.5708rad)
  sketch-geometry (2):
    g0: Circle CenterX=34 CenterY=14 CenterZ=0 NormalX=0 NormalY=0 NormalZ=1 AngleXU=0 Radius=1.3
    g1: Circle CenterX=34 CenterY=31 CenterZ=0 NormalX=0 NormalY=0 NormalZ=1 AngleXU=0 Radius=1.3
  constraints (6):
    c: Diameter(g0) = 2.6
    c: Diameter(g1) = 2.6
    c: DistanceY(g1,g-5) = 10
    c: DistanceY(g-5,g0) = 10
    c: DistanceX(g0,g-5) = 10
    c: DistanceX(g1,g-5) = 10
FEATURE [PartDesign::Pocket] Pocket009
  BaseFeature = -> Pocket008
  Direction = (0,1,-2e-16)
  Length = 10
  Length2 = 5
  Profile = -> Sketch013
  ReferenceAxis = -> Sketch013 [N_Axis]
  Refine = true
  Suppressed = false
  Type = 0
FEATURE [Sketcher::SketchObject] Sketch014
  ArcFitTolerance = 1e-06
  AttachmentSupport = -> [Pocket009]
  ExternalGeometry = -> [Pocket009]
  FullyConstrained = true
  MakeInternals = false
  MapMode = 5
  Placement = pos=(0,85,0) rot=(1,0,0;1.5708rad)
  sketch-geometry (1):
    g0: Circle CenterX=34 CenterY=37.5 CenterZ=0 NormalX=0 NormalY=0 NormalZ=1 AngleXU=0 Radius=1.3
  constraints (3):
    c: Diameter(g0) = 2.6
    c: DistanceY(g0,g-3) = 3.5
    c: DistanceX(g0,g-3) = 10
FEATURE [PartDesign::Pocket] Pocket010
  BaseFeature = -> Pocket009
  Direction = (0,1,-2e-16)
  Length = 5
  Length2 = 5
  Profile = -> Sketch014
  ReferenceAxis = -> Sketch014 [N_Axis]
  Refine = true
  Suppressed = false
  Type = 0
FEATURE [PartDesign::Body] Body003  label="left-split"
  AllowCompound = false
  Group = -> [Clone,Sketch012,Pocket008,Sketch013,Pocket009,Sketch014,Pocket010]
  Origin = -> Origin007
  Tip = -> Pocket010
PROVENANCE & LICENSES
A FreeCAD (.FCStd) document from a public repository crawl; recipes are the document's own serialized feature recipes (and, for linked parts, companion documents' recipes).
License: as declared in the source repository (recorded in the dataset sidecar).
